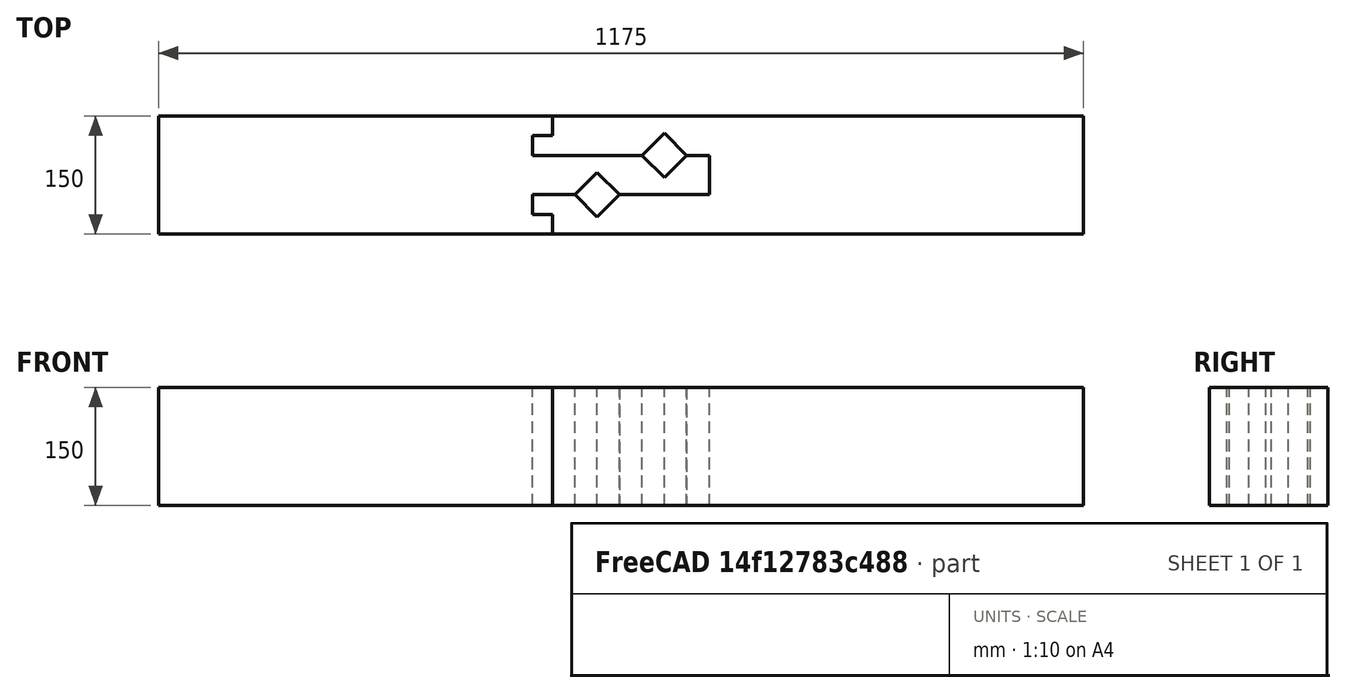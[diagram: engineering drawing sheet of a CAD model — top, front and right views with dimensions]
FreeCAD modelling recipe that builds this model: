
FCSTD DOCUMENT  (FreeCAD 0.18R13516 (Git))
Label: VIGA MADEIRA EMENDA 3
License: All rights reserved
LicenseURL: http://en.wikipedia.org/wiki/All_rights_reserved
objects: Part::Cut×9, PartDesign::FeatureBase×8, Part::Box×5
note: 22 computed .brp shape members not serialized (recipe doc carries the construction recipe); baked Part::Feature solids carry a one-line shape summary decoded from their .brp

FEATURE [Part::Box] Box  label="Cube"
  AttacherType = Attacher::AttachEngine3D
  Height = 150
  Length = 700
  Placement = pos=(-500,0,0) rot=(0,0,1;0rad)
  Width = 150
FEATURE [Part::Box] Box001  label="Cube001"
  AttacherType = Attacher::AttachEngine3D
  Height = 150
  Length = 200
  Width = 25
FEATURE [Part::Box] Box002  label="Cube002"
  AttacherType = Attacher::AttachEngine3D
  Height = 150
  Length = 225
  Placement = pos=(-25,25,0) rot=(0,0,1;0rad)
  Width = 25
FEATURE [PartDesign::FeatureBase] Clone
  BaseFeature = -> Box001
  Placement = pos=(0,125,0) rot=(0,0,1;0rad)
FEATURE [PartDesign::FeatureBase] Clone001
  BaseFeature = -> Box002
  Placement = pos=(-25,100,0) rot=(0,0,1;0rad)
FEATURE [Part::Box] Box003  label="Cube003"
  AttacherType = Attacher::AttachEngine3D
  Height = 150
  Length = 40
  Placement = pos=(57.06,21.71,0) rot=(0,0,1;0.785398rad)
  Width = 40
FEATURE [PartDesign::FeatureBase] Clone002
  BaseFeature = -> Box003
  Placement = pos=(142.4,71.7,0) rot=(0,0,1;0.785398rad)
FEATURE [PartDesign::FeatureBase] Clone003
  BaseFeature = -> Box003
  Placement = pos=(57.06,21.71,0) rot=(0,0,1;0.785398rad)
FEATURE [PartDesign::FeatureBase] Clone004
  BaseFeature = -> Clone002
  Placement = pos=(142.4,71.7,0) rot=(0,0,1;0.785398rad)
FEATURE [Part::Cut] Cut
  Base = -> Box
  Tool = -> Box001
FEATURE [Part::Cut] Cut001
  Base = -> Cut
  Tool = -> Box002
FEATURE [Part::Cut] Cut002
  Base = -> Cut001
  Tool = -> Clone
FEATURE [Part::Cut] Cut003
  Base = -> Cut002
  Tool = -> Clone001
FEATURE [Part::Cut] Cut004
  Base = -> Cut003
  Tool = -> Box003
FEATURE [Part::Cut] Cut005
  Base = -> Cut004
  Tool = -> Clone002
FEATURE [Part::Box] Box004  label="Cube004"
  AttacherType = Attacher::AttachEngine3D
  Height = 150
  Length = 700
  Placement = pos=(-25,0,0) rot=(0,0,1;0rad)
  Width = 150
FEATURE [PartDesign::FeatureBase] Clone005
  BaseFeature = -> Cut005
FEATURE [Part::Cut] Cut006
  Base = -> Box004
  Tool = -> Cut005
FEATURE [PartDesign::FeatureBase] Clone006
  BaseFeature = -> Clone003
  Placement = pos=(57.06,21.71,0) rot=(0,0,1;0.785398rad)
FEATURE [PartDesign::FeatureBase] Clone007
  BaseFeature = -> Clone004
  Placement = pos=(142.4,71.7,0) rot=(0,0,1;0.785398rad)
FEATURE [Part::Cut] Cut007
  Base = -> Cut006
  Tool = -> Clone003
FEATURE [Part::Cut] Cut008
  Base = -> Cut007
  Tool = -> Clone004
